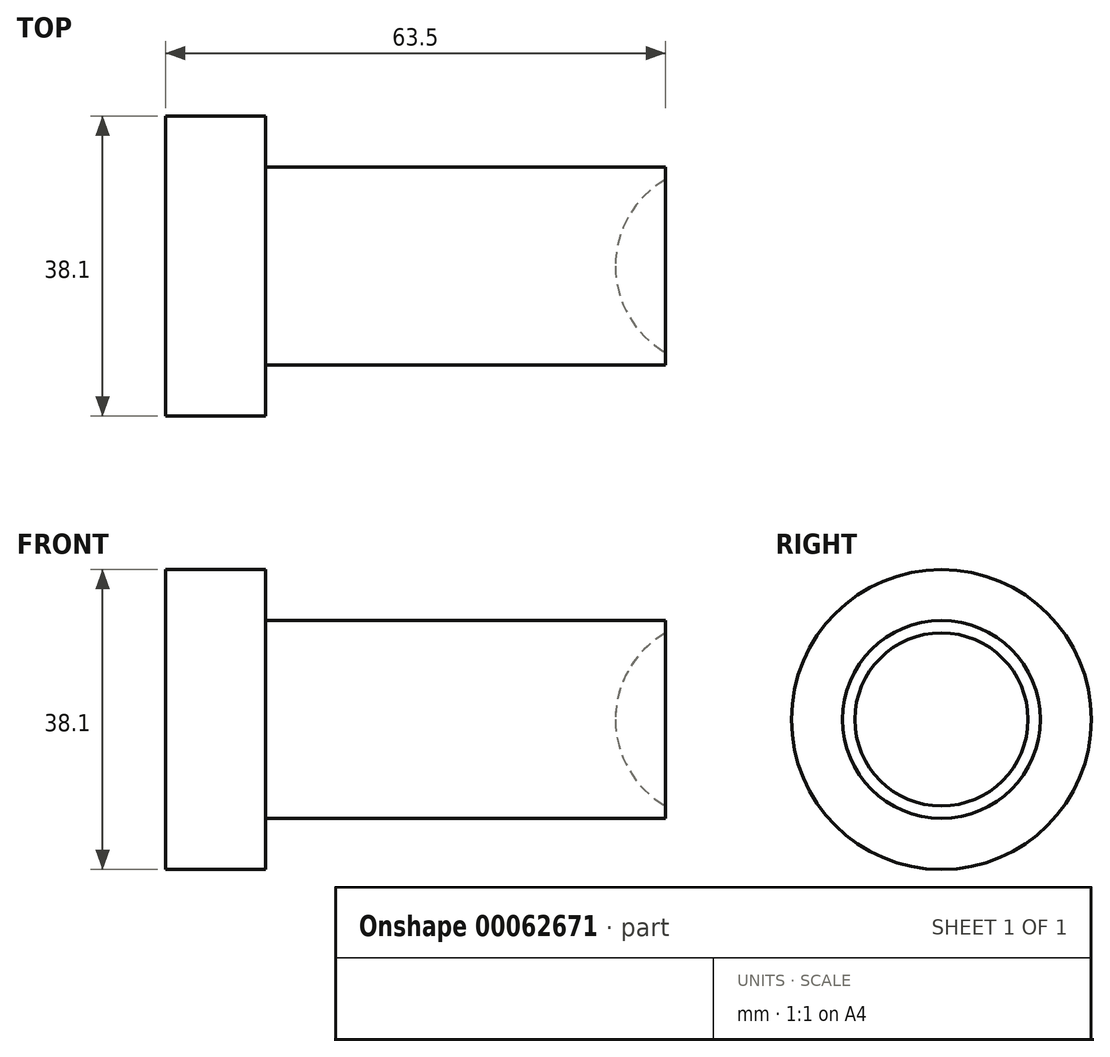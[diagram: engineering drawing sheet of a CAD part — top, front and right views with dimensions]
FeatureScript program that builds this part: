
annotation { "Feature Type Name" : "Feature", "Feature Type Description" : "" }
export const myFeature = defineFeature(function(context is Context, id is Id, definition is map)
    precondition{}
    {
        {
            var Q0;
            Q0=qCreatedBy(makeId("Front.planeOp"),FACE);
            var sketch = newSketch(context, id + "F0", { "sketchPlane" : qUnion([Q0])});
            skLineSegment(sketch, "E0.bottom", {"start": v(0, 0) * mm, "end": v(12.7, 0) * mm});
            skLineSegment(sketch, "E0.top", {"start": v(0, 19.05) * mm, "end": v(12.7, 19.05) * mm});
            skLineSegment(sketch, "E0.left", {"start": v(0, 0) * mm, "end": v(0, 19.05) * mm});
            skLineSegment(sketch, "E0.right", {"start": v(12.7, 0) * mm, "end": v(12.7, 19.05) * mm});
            skLineSegment(sketch, "E1.bottom", {"start": v(12.7, 0) * mm, "end": v(57.15, 0) * mm});
            skLineSegment(sketch, "E1.top", {"start": v(12.7, 12.57) * mm, "end": v(63.5, 12.57) * mm});
            skLineSegment(sketch, "E1.left", {"start": v(12.7, 0) * mm, "end": v(12.7, 12.57) * mm});
            skLineSegment(sketch, "E1.right", {"start": v(63.5, 11) * mm, "end": v(63.5, 12.57) * mm});
            skArc(sketch, "E2", {"start": v(63.5, 11) * mm, "mid": v(58.85, 6.35) * mm, "end": v(57.15, 0) * mm});
            skPoint(sketch, "E3.orphan", {"position": v(63.5, 0) * mm});
            skSolve(sketch);
        }
        {
            var Q0;
            Q0=makeQuery(id+"F0.imprint","IMPRINT",FACE,{"disambiguationData":[TD([[makeQuery(id+"F0.imprint","IMPRINT",EDGE,{"derivedFrom":sQuery(id+"F0.wireOp",EDGE,"E0.bottom")}),1.0]])]});
            var Q1;
            Q1=makeQuery(id+"F0.imprint","IMPRINT",FACE,{"disambiguationData":[TD([[makeQuery(id+"F0.imprint","IMPRINT",EDGE,{"derivedFrom":sQuery(id+"F0.wireOp",EDGE,"E1.bottom")}),1.0]])]});
            var Q2;
            Q2=sQuery(id+"F0.wireOp",EDGE,"E1.bottom");
            revolve(context, id + "F1", {"entities" : qUnion([Q0, Q1]), "axis" : qUnion([Q2]), "revolveType" : RevolveType.FULL});
        }
    });
